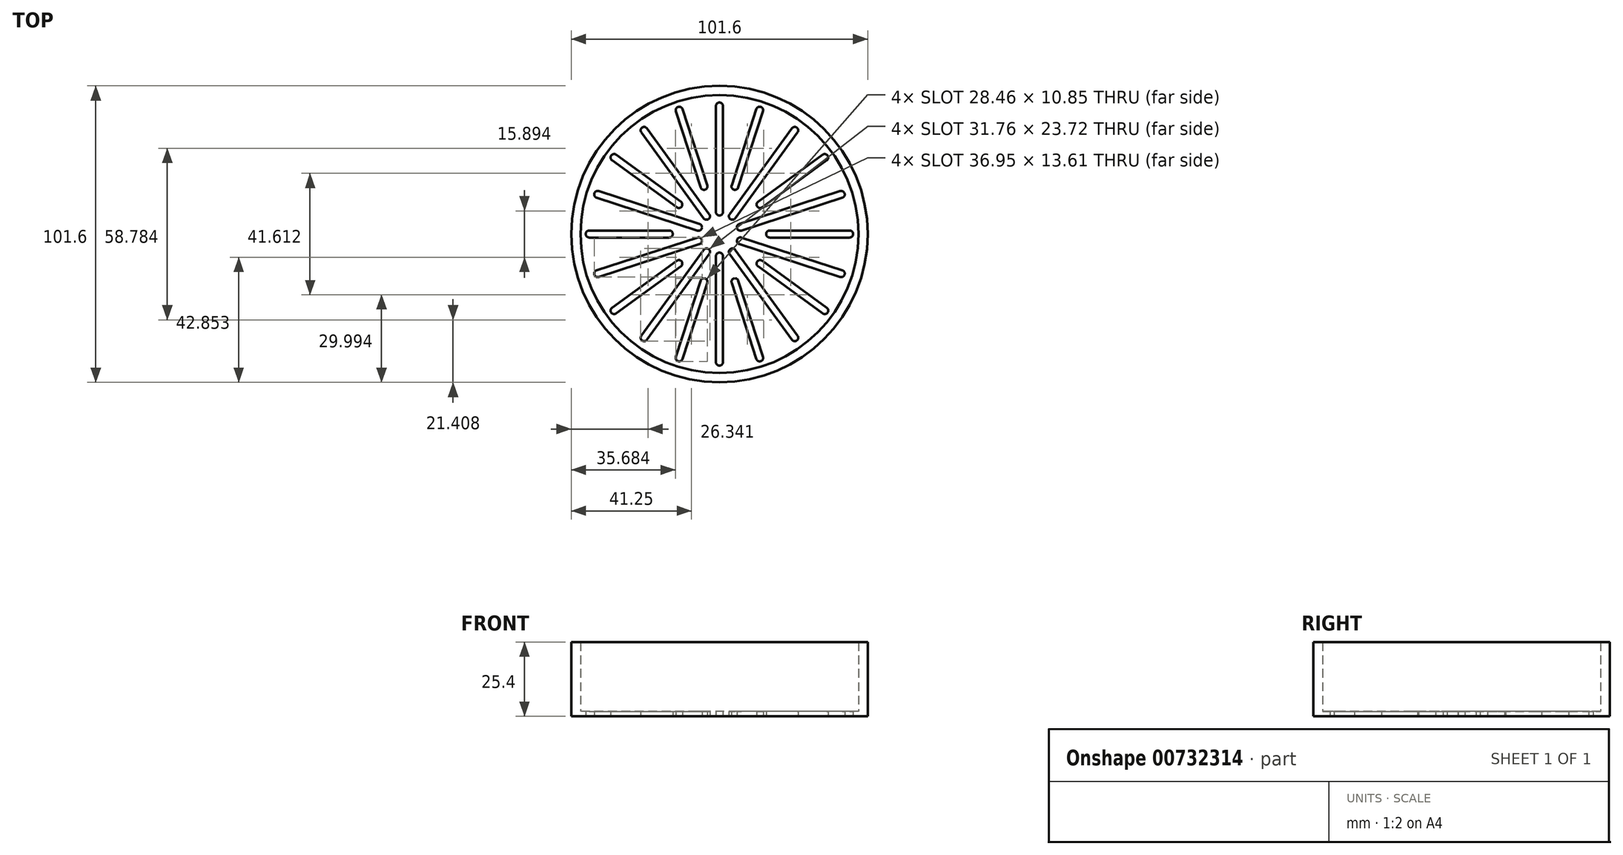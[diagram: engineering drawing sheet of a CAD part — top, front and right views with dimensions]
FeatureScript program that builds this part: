
annotation { "Feature Type Name" : "Feature", "Feature Type Description" : "" }
export const myFeature = defineFeature(function(context is Context, id is Id, definition is map)
    precondition{}
    {
        {
            var Q0;
            Q0=qCreatedBy(makeId("Top.planeOp"),FACE);
            var sketch = newSketch(context, id + "F0", { "sketchPlane" : qUnion([Q0])});
            skCircle(sketch, "E0", {"center": v(0, 0) * mm, "radius": 50.8 * mm});
            skLineSegment(sketch, "E1", {"start": v(1.2, 43.9) * mm, "end": v(1.2, 7.54) * mm});
            skCircle(sketch, "E2", {"center": v(0, 0) * mm, "radius": 47.63 * mm});
            skLineSegment(sketch, "E3", {"start": v(-1.2, 43.9) * mm, "end": v(-1.2, 7.54) * mm});
            skArc(sketch, "E4", {"start": v(1.2, 43.9) * mm, "mid": v(0, 45.09) * mm, "end": v(-1.2, 43.9) * mm});
            skArc(sketch, "E5", {"start": v(-1.2, 7.54) * mm, "mid": v(0, 6.35) * mm, "end": v(1.2, 7.54) * mm});
            skLineSegment(sketch, "E6", {"start": v(13.79, 42.44) * mm, "end": v(0, 0) * mm, "construction": true});
            skArc(sketch, "E7", {"start": v(14.92, 42.07) * mm, "mid": v(14.16, 43.57) * mm, "end": v(12.66, 42.8) * mm});
            skArc(sketch, "E8", {"start": v(4.18, 16.72) * mm, "mid": v(4.94, 15.22) * mm, "end": v(6.44, 15.98) * mm});
            skLineSegment(sketch, "E9", {"start": v(6.44, 15.98) * mm, "end": v(14.92, 42.07) * mm});
            skLineSegment(sketch, "E10", {"start": v(12.66, 42.8) * mm, "end": v(4.18, 16.72) * mm});
            skArc(sketch, "E11.1.0", {"start": v(-5.4, 5.4) * mm, "mid": v(-3.73, 5.14) * mm, "end": v(-3.47, 6.8) * mm});
            skLineSegment(sketch, "E11.1.1", {"start": v(-26.76, 34.81) * mm, "end": v(-5.4, 5.4) * mm});
            skLineSegment(sketch, "E11.1.2", {"start": v(-24.84, 36.21) * mm, "end": v(-3.47, 6.8) * mm});
            skLineSegment(sketch, "E11.1.3", {"start": v(-4.18, 16.72) * mm, "end": v(-12.66, 42.8) * mm});
            skLineSegment(sketch, "E11.1.4", {"start": v(-14.92, 42.07) * mm, "end": v(-6.44, 15.98) * mm});
            skArc(sketch, "E11.1.5", {"start": v(-24.84, 36.21) * mm, "mid": v(-26.5, 36.47) * mm, "end": v(-26.76, 34.81) * mm});
            skArc(sketch, "E11.1.6", {"start": v(-6.44, 15.98) * mm, "mid": v(-4.94, 15.22) * mm, "end": v(-4.18, 16.72) * mm});
            skArc(sketch, "E11.1.7", {"start": v(-12.66, 42.8) * mm, "mid": v(-14.16, 43.57) * mm, "end": v(-14.92, 42.07) * mm});
            skArc(sketch, "E11.2.0", {"start": v(-7.54, 1.2) * mm, "mid": v(-6.04, 1.96) * mm, "end": v(-6.8, 3.46) * mm});
            skLineSegment(sketch, "E11.2.1", {"start": v(-42.11, 12.43) * mm, "end": v(-7.54, 1.2) * mm});
            skLineSegment(sketch, "E11.2.2", {"start": v(-41.38, 14.7) * mm, "end": v(-6.8, 3.46) * mm});
            skLineSegment(sketch, "E11.2.3", {"start": v(-13.2, 11.07) * mm, "end": v(-35.4, 27.19) * mm});
            skLineSegment(sketch, "E11.2.4", {"start": v(-36.8, 25.26) * mm, "end": v(-14.6, 9.14) * mm});
            skArc(sketch, "E11.2.5", {"start": v(-41.38, 14.7) * mm, "mid": v(-42.88, 13.93) * mm, "end": v(-42.11, 12.43) * mm});
            skArc(sketch, "E11.2.6", {"start": v(-14.6, 9.14) * mm, "mid": v(-12.94, 9.4) * mm, "end": v(-13.2, 11.07) * mm});
            skArc(sketch, "E11.2.7", {"start": v(-35.4, 27.19) * mm, "mid": v(-37.06, 26.93) * mm, "end": v(-36.8, 25.26) * mm});
            skArc(sketch, "E11.3.0", {"start": v(-6.8, -3.46) * mm, "mid": v(-6.04, -1.96) * mm, "end": v(-7.54, -1.2) * mm});
            skLineSegment(sketch, "E11.3.1", {"start": v(-41.38, -14.7) * mm, "end": v(-6.8, -3.46) * mm});
            skLineSegment(sketch, "E11.3.2", {"start": v(-42.11, -12.43) * mm, "end": v(-7.54, -1.2) * mm});
            skLineSegment(sketch, "E11.3.3", {"start": v(-17.19, 1.2) * mm, "end": v(-44.62, 1.2) * mm});
            skLineSegment(sketch, "E11.3.4", {"start": v(-44.62, -1.2) * mm, "end": v(-17.19, -1.2) * mm});
            skArc(sketch, "E11.3.5", {"start": v(-42.11, -12.43) * mm, "mid": v(-42.88, -13.93) * mm, "end": v(-41.38, -14.7) * mm});
            skArc(sketch, "E11.3.6", {"start": v(-17.19, -1.2) * mm, "mid": v(-16, 0) * mm, "end": v(-17.19, 1.2) * mm});
            skArc(sketch, "E11.3.7", {"start": v(-44.62, 1.2) * mm, "mid": v(-45.81, 0) * mm, "end": v(-44.62, -1.2) * mm});
            skArc(sketch, "E11.4.0", {"start": v(-3.47, -6.8) * mm, "mid": v(-3.73, -5.14) * mm, "end": v(-5.4, -5.4) * mm});
            skLineSegment(sketch, "E11.4.1", {"start": v(-24.84, -36.21) * mm, "end": v(-3.47, -6.8) * mm});
            skLineSegment(sketch, "E11.4.2", {"start": v(-26.76, -34.81) * mm, "end": v(-5.4, -5.4) * mm});
            skLineSegment(sketch, "E11.4.3", {"start": v(-14.6, -9.14) * mm, "end": v(-36.8, -25.26) * mm});
            skLineSegment(sketch, "E11.4.4", {"start": v(-35.4, -27.19) * mm, "end": v(-13.2, -11.07) * mm});
            skArc(sketch, "E11.4.5", {"start": v(-26.76, -34.81) * mm, "mid": v(-26.5, -36.47) * mm, "end": v(-24.84, -36.21) * mm});
            skArc(sketch, "E11.4.6", {"start": v(-13.2, -11.07) * mm, "mid": v(-12.94, -9.4) * mm, "end": v(-14.6, -9.14) * mm});
            skArc(sketch, "E11.4.7", {"start": v(-36.8, -25.26) * mm, "mid": v(-37.06, -26.93) * mm, "end": v(-35.4, -27.19) * mm});
            skArc(sketch, "E11.5.0", {"start": v(1.2, -7.54) * mm, "mid": v(0, -6.35) * mm, "end": v(-1.2, -7.54) * mm});
            skLineSegment(sketch, "E11.5.1", {"start": v(1.2, -43.9) * mm, "end": v(1.2, -7.54) * mm});
            skLineSegment(sketch, "E11.5.2", {"start": v(-1.2, -43.9) * mm, "end": v(-1.2, -7.54) * mm});
            skLineSegment(sketch, "E11.5.3", {"start": v(-6.44, -15.98) * mm, "end": v(-14.92, -42.07) * mm});
            skLineSegment(sketch, "E11.5.4", {"start": v(-12.66, -42.8) * mm, "end": v(-4.18, -16.72) * mm});
            skArc(sketch, "E11.5.5", {"start": v(-1.2, -43.9) * mm, "mid": v(0, -45.09) * mm, "end": v(1.2, -43.9) * mm});
            skArc(sketch, "E11.5.6", {"start": v(-4.18, -16.72) * mm, "mid": v(-4.94, -15.22) * mm, "end": v(-6.44, -15.98) * mm});
            skArc(sketch, "E11.5.7", {"start": v(-14.92, -42.07) * mm, "mid": v(-14.16, -43.57) * mm, "end": v(-12.66, -42.8) * mm});
            skArc(sketch, "E11.6.0", {"start": v(5.4, -5.4) * mm, "mid": v(3.73, -5.14) * mm, "end": v(3.47, -6.8) * mm});
            skLineSegment(sketch, "E11.6.1", {"start": v(26.76, -34.81) * mm, "end": v(5.4, -5.4) * mm});
            skLineSegment(sketch, "E11.6.2", {"start": v(24.84, -36.21) * mm, "end": v(3.47, -6.8) * mm});
            skLineSegment(sketch, "E11.6.3", {"start": v(4.18, -16.72) * mm, "end": v(12.66, -42.8) * mm});
            skLineSegment(sketch, "E11.6.4", {"start": v(14.92, -42.07) * mm, "end": v(6.44, -15.98) * mm});
            skArc(sketch, "E11.6.5", {"start": v(24.84, -36.21) * mm, "mid": v(26.5, -36.47) * mm, "end": v(26.76, -34.81) * mm});
            skArc(sketch, "E11.6.6", {"start": v(6.44, -15.98) * mm, "mid": v(4.94, -15.22) * mm, "end": v(4.18, -16.72) * mm});
            skArc(sketch, "E11.6.7", {"start": v(12.66, -42.8) * mm, "mid": v(14.16, -43.57) * mm, "end": v(14.92, -42.07) * mm});
            skArc(sketch, "E11.7.0", {"start": v(7.54, -1.2) * mm, "mid": v(6.04, -1.96) * mm, "end": v(6.8, -3.46) * mm});
            skLineSegment(sketch, "E11.7.1", {"start": v(42.11, -12.43) * mm, "end": v(7.54, -1.2) * mm});
            skLineSegment(sketch, "E11.7.2", {"start": v(41.38, -14.7) * mm, "end": v(6.8, -3.46) * mm});
            skLineSegment(sketch, "E11.7.3", {"start": v(13.2, -11.07) * mm, "end": v(35.4, -27.19) * mm});
            skLineSegment(sketch, "E11.7.4", {"start": v(36.8, -25.26) * mm, "end": v(14.6, -9.14) * mm});
            skArc(sketch, "E11.7.5", {"start": v(41.38, -14.7) * mm, "mid": v(42.88, -13.93) * mm, "end": v(42.11, -12.43) * mm});
            skArc(sketch, "E11.7.6", {"start": v(14.6, -9.14) * mm, "mid": v(12.94, -9.4) * mm, "end": v(13.2, -11.07) * mm});
            skArc(sketch, "E11.7.7", {"start": v(35.4, -27.19) * mm, "mid": v(37.06, -26.93) * mm, "end": v(36.8, -25.26) * mm});
            skArc(sketch, "E11.8.0", {"start": v(6.8, 3.46) * mm, "mid": v(6.04, 1.96) * mm, "end": v(7.54, 1.2) * mm});
            skLineSegment(sketch, "E11.8.1", {"start": v(41.38, 14.7) * mm, "end": v(6.8, 3.46) * mm});
            skLineSegment(sketch, "E11.8.2", {"start": v(42.11, 12.43) * mm, "end": v(7.54, 1.2) * mm});
            skLineSegment(sketch, "E11.8.3", {"start": v(17.19, -1.2) * mm, "end": v(44.62, -1.2) * mm});
            skLineSegment(sketch, "E11.8.4", {"start": v(44.62, 1.2) * mm, "end": v(17.19, 1.2) * mm});
            skArc(sketch, "E11.8.5", {"start": v(42.11, 12.43) * mm, "mid": v(42.88, 13.93) * mm, "end": v(41.38, 14.7) * mm});
            skArc(sketch, "E11.8.6", {"start": v(17.19, 1.2) * mm, "mid": v(16, 0) * mm, "end": v(17.19, -1.2) * mm});
            skArc(sketch, "E11.8.7", {"start": v(44.62, -1.2) * mm, "mid": v(45.81, 0) * mm, "end": v(44.62, 1.2) * mm});
            skArc(sketch, "E11.9.0", {"start": v(3.47, 6.8) * mm, "mid": v(3.73, 5.14) * mm, "end": v(5.4, 5.4) * mm});
            skLineSegment(sketch, "E11.9.1", {"start": v(24.84, 36.21) * mm, "end": v(3.47, 6.8) * mm});
            skLineSegment(sketch, "E11.9.2", {"start": v(26.76, 34.81) * mm, "end": v(5.4, 5.4) * mm});
            skLineSegment(sketch, "E11.9.3", {"start": v(14.6, 9.14) * mm, "end": v(36.8, 25.26) * mm});
            skLineSegment(sketch, "E11.9.4", {"start": v(35.4, 27.19) * mm, "end": v(13.2, 11.07) * mm});
            skArc(sketch, "E11.9.5", {"start": v(26.76, 34.81) * mm, "mid": v(26.5, 36.47) * mm, "end": v(24.84, 36.21) * mm});
            skArc(sketch, "E11.9.6", {"start": v(13.2, 11.07) * mm, "mid": v(12.94, 9.4) * mm, "end": v(14.6, 9.14) * mm});
            skArc(sketch, "E11.9.7", {"start": v(36.8, 25.26) * mm, "mid": v(37.06, 26.93) * mm, "end": v(35.4, 27.19) * mm});
            skSolve(sketch);
        }
        {
            var Q0;
            Q0=makeQuery(id+"F0.imprint","IMPRINT",FACE,{"disambiguationData":[TD([[makeQuery(id+"F0.imprint","IMPRINT",EDGE,{"derivedFrom":sQuery(id+"F0.wireOp",EDGE,"E1")}),1.0]])]});
            extrude(context, id + "F1", {"entities" : qUnion([Q0]), "depth" : 1.59 * mm, "offsetDistance" : 25.4 * mm});
        }
        {
            var Q0;
            Q0=makeQuery(id+"F0.imprint","IMPRINT",FACE,{"disambiguationData":[TD([[makeQuery(id+"F0.imprint","IMPRINT",EDGE,{"derivedFrom":sQuery(id+"F0.wireOp",EDGE,"E0")}),1.0]])]});
            extrude(context, id + "F2", {"entities" : qUnion([Q0]), "operationType" : NewBodyOperationType.ADD, "depth" : 25.4 * mm, "offsetDistance" : 25.4 * mm});
        }
    });
